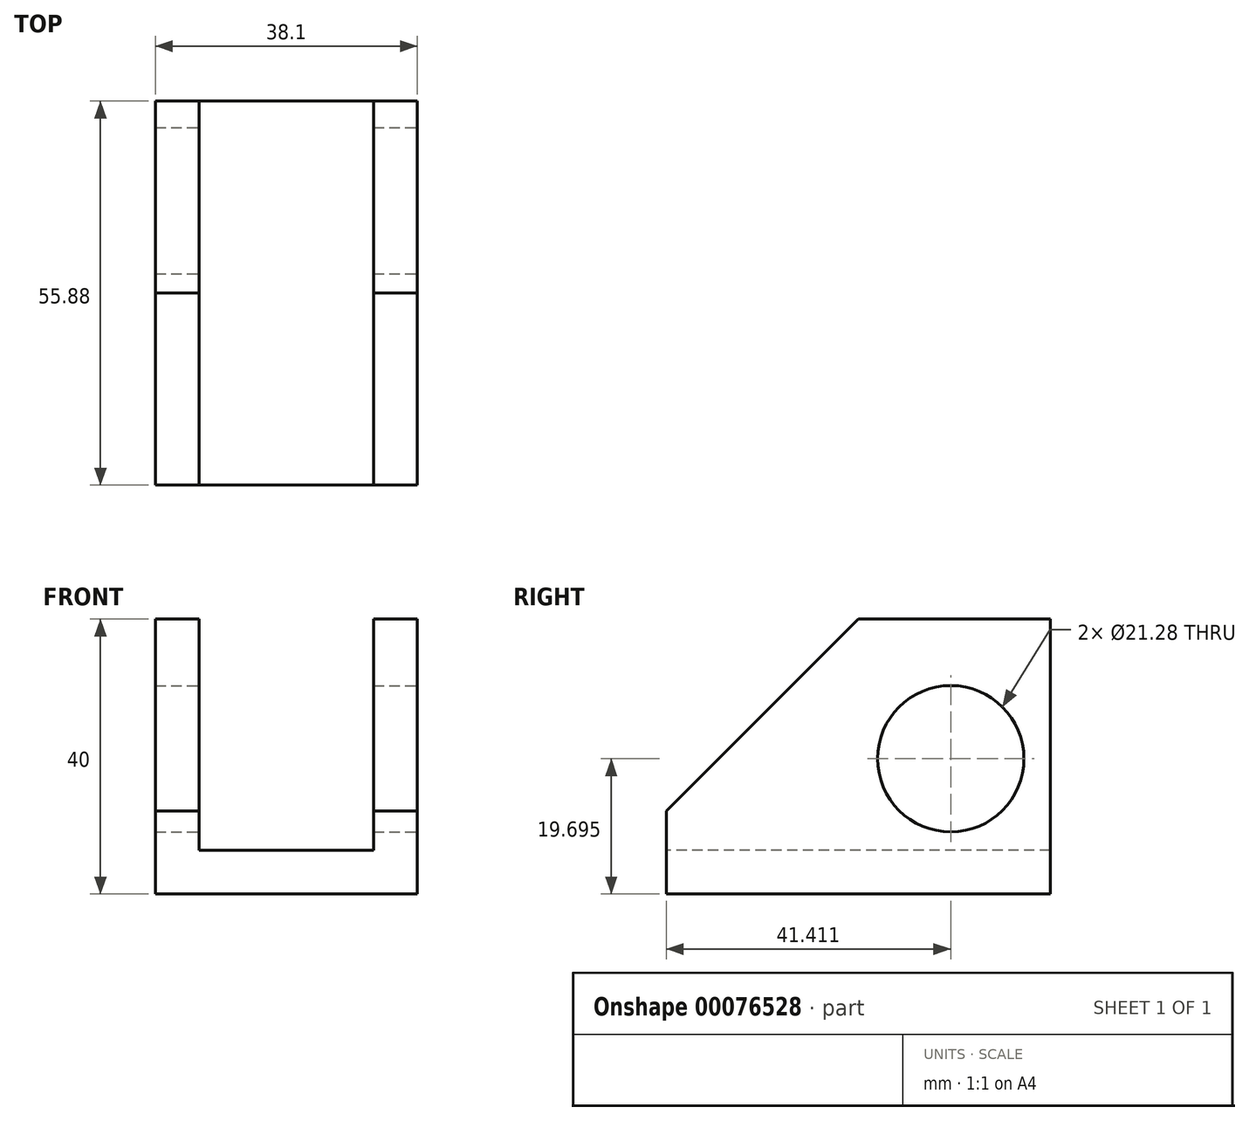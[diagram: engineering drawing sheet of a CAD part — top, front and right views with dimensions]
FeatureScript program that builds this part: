
annotation { "Feature Type Name" : "Feature", "Feature Type Description" : "" }
export const myFeature = defineFeature(function(context is Context, id is Id, definition is map)
    precondition{}
    {
        {
            var Q0;
            Q0=qCreatedBy(makeId("Top.planeOp"),FACE);
            var sketch = newSketch(context, id + "F0", { "sketchPlane" : qUnion([Q0])});
            skLineSegment(sketch, "E0", {"start": v(0, 27.94) * mm, "end": v(19.05, 27.94) * mm});
            skLineSegment(sketch, "E1", {"start": v(19.05, 27.94) * mm, "end": v(19.05, 0) * mm});
            skLineSegment(sketch, "E2.MirrorCS", {"start": v(0, -27.94) * mm, "end": v(19.05, -27.94) * mm});
            skLineSegment(sketch, "E3.MirrorCS", {"start": v(19.05, -27.94) * mm, "end": v(19.05, 0) * mm});
            skLineSegment(sketch, "E4.MirrorCS", {"start": v(0, -27.94) * mm, "end": v(-19.05, -27.94) * mm});
            skLineSegment(sketch, "E5.MirrorCS", {"start": v(-19.05, -27.94) * mm, "end": v(-19.05, 0) * mm});
            skLineSegment(sketch, "E6.MirrorCS", {"start": v(0, 27.94) * mm, "end": v(-19.05, 27.94) * mm});
            skLineSegment(sketch, "E7.MirrorCS", {"start": v(-19.05, 27.94) * mm, "end": v(-19.05, 0) * mm});
            skSolve(sketch);
        }
        {
            var Q0;
            Q0=makeQuery(id+"F0.imprint","IMPRINT",FACE,{"disambiguationData":[TD([[makeQuery(id+"F0.imprint","IMPRINT",EDGE,{"derivedFrom":sQuery(id+"F0.wireOp",EDGE,"E0")}),-1.0]])]});
            extrude(context, id + "F1", {"entities" : qUnion([Q0]), "depth" : 6.35 * mm});
        }
        {
            var Q0;
            Q0=makeQuery(id+"F1.opExtrude","CAP_FACE",FACE,{"disambiguationData":[OSD([sQuery(id+"F0.wireOp",EDGE,"E0"),sQuery(id+"F0.wireOp",EDGE,"E1"),sQuery(id+"F0.wireOp",EDGE,"E2.MirrorCS"),sQuery(id+"F0.wireOp",EDGE,"E3.MirrorCS"),sQuery(id+"F0.wireOp",EDGE,"E4.MirrorCS"),sQuery(id+"F0.wireOp",EDGE,"E5.MirrorCS"),sQuery(id+"F0.wireOp",EDGE,"E6.MirrorCS"),sQuery(id+"F0.wireOp",EDGE,"E7.MirrorCS")])],"isStart":false});
            var sketch = newSketch(context, id + "F2", { "sketchPlane" : qUnion([Q0])});
            skLineSegment(sketch, "E8", {"start": v(-12.7, 27.94) * mm, "end": v(-12.7, -27.94) * mm});
            skLineSegment(sketch, "E9.MirrorCS", {"start": v(12.7, 27.94) * mm, "end": v(12.7, -27.94) * mm});
            skSolve(sketch);
        }
        {
            var Q0;
            {var subQ0=sQuery(id+"F2.wireOp",EDGE,"E8");Q0=makeQuery(id+"F2.imprint","IMPRINT",FACE,{"disambiguationData":[TD([[makeQuery(id+"F2.imprint","IMPRINT",EDGE,{"derivedFrom":subQ0}),-1.0]])]});}
            var Q1;
            {var subQ0=sQuery(id+"F2.wireOp",EDGE,"E9.MirrorCS");Q1=makeQuery(id+"F2.imprint","IMPRINT",FACE,{"disambiguationData":[TD([[makeQuery(id+"F2.imprint","IMPRINT",EDGE,{"derivedFrom":subQ0}),1.0]])]});}
            extrude(context, id + "F3", {"entities" : qUnion([Q0, Q1]), "operationType" : NewBodyOperationType.ADD, "depth" : 33.65 * mm});
        }
        {
            var Q0;
            {var subQ0=sQuery(id+"F0.wireOp",EDGE,"E4.MirrorCS");var subQ1=sQuery(id+"F0.wireOp",EDGE,"E2.MirrorCS");var subQ2=makeQuery(id+"F1.opExtrude","CAP_EDGE",EDGE,{"disambiguationData":[OSD([subQ1,subQ0])],"isStart":false});Q0=makeQuery(id+"F3.opExtrude","CAP_EDGE",EDGE,{"disambiguationData":[OSD([subQ1,subQ0]),TDD([makeQuery(id+"F2.imprint","IMPRINT",EDGE,{"disambiguationData":[TD([[makeQuery(id+"F2.imprint","INTERSECT",VERTEX,{"derivedFrom":[subQ2,sQuery(id+"F2.wireOp",EDGE,"E9.MirrorCS")]}),1.0]])],"derivedFrom":subQ2})])],"isStart":false});}
            var Q1;
            {var subQ0=sQuery(id+"F0.wireOp",EDGE,"E4.MirrorCS");var subQ1=sQuery(id+"F0.wireOp",EDGE,"E2.MirrorCS");var subQ2=makeQuery(id+"F1.opExtrude","CAP_EDGE",EDGE,{"disambiguationData":[OSD([subQ1,subQ0])],"isStart":false});Q1=makeQuery(id+"F3.opExtrude","CAP_EDGE",EDGE,{"disambiguationData":[OSD([subQ1,subQ0]),TDD([makeQuery(id+"F2.imprint","IMPRINT",EDGE,{"disambiguationData":[TD([[makeQuery(id+"F2.imprint","INTERSECT",VERTEX,{"derivedFrom":[subQ2,sQuery(id+"F2.wireOp",EDGE,"E8")]}),-1.0]])],"derivedFrom":subQ2})])],"isStart":false});}
            chamfer(context, id + "F4", {"entities" : qUnion([Q0, Q1]), "width" : 27.94 * mm, "tangentPropagation" : true});
        }
        {
            var Q0;
            {var subQ0=sQuery(id+"F0.wireOp",EDGE,"E3.MirrorCS");var subQ1=sQuery(id+"F0.wireOp",EDGE,"E1");Q0=makeQuery(id+"F3.boolean.opBoolean","MERGE",FACE,{"derivedFrom":[makeQuery(id+"F1.opExtrude","SWEPT_FACE",FACE,{"disambiguationData":[OSD([subQ1,subQ0])]}),makeQuery(id+"F3.opExtrude","SWEPT_FACE",FACE,{"disambiguationData":[OSD([subQ1,subQ0])]})]});}
            var sketch = newSketch(context, id + "F5", { "sketchPlane" : qUnion([Q0])});
            skCircle(sketch, "E10", {"center": v(13.47, 19.7) * mm, "radius": 10.64 * mm});
            skSolve(sketch);
        }
        {
            var Q0;
            Q0=makeQuery(id+"F5.imprint","IMPRINT",FACE,{"disambiguationData":[TD([[makeQuery(id+"F5.imprint","IMPRINT",EDGE,{"derivedFrom":sQuery(id+"F5.wireOp",EDGE,"E10")}),1.0]])]});
            extrude(context, id + "F6", {"entities" : qUnion([Q0]), "operationType" : NewBodyOperationType.REMOVE, "endBound" : BoundingType.THROUGH_ALL, "oppositeDirection" : true, "depth" : 25.4 * mm});
        }
    });
